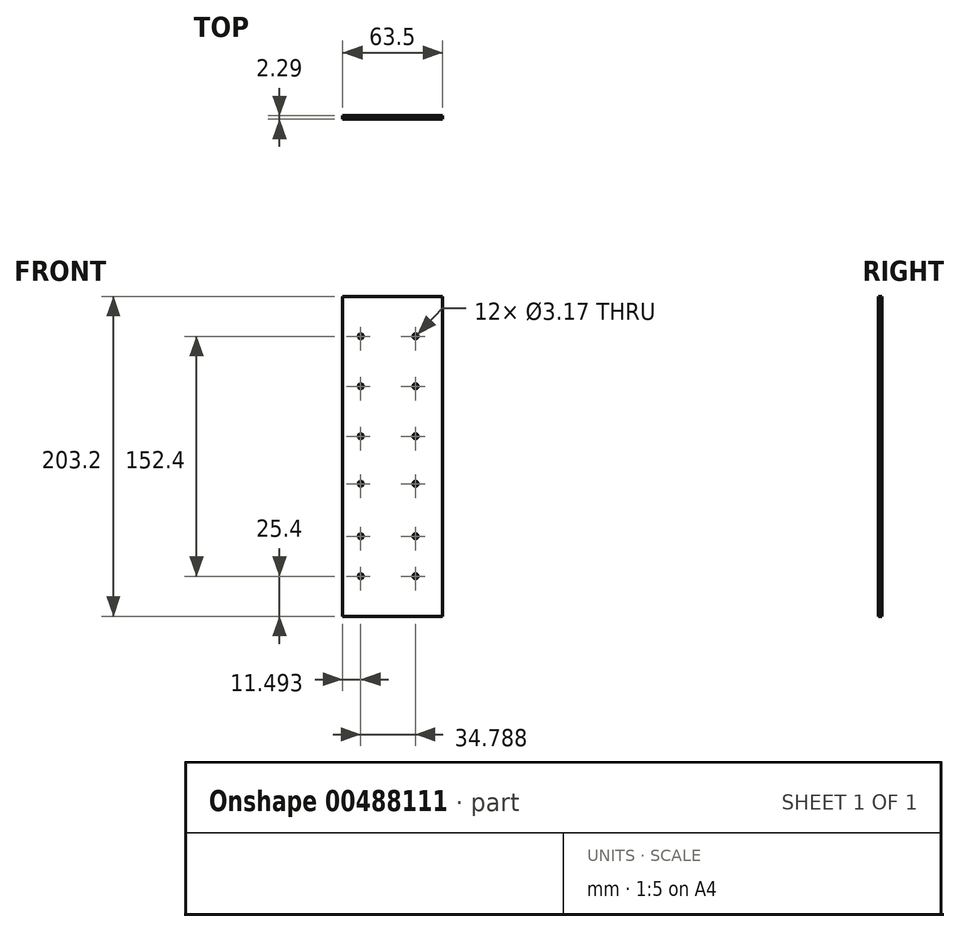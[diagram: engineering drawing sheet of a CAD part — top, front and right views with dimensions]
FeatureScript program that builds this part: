
annotation { "Feature Type Name" : "Feature", "Feature Type Description" : "" }
export const myFeature = defineFeature(function(context is Context, id is Id, definition is map)
    precondition{}
    {
        {
            var Q0;
            Q0=qCreatedBy(makeId("Front.planeOp"),FACE);
            var sketch = newSketch(context, id + "F0", { "sketchPlane" : qUnion([Q0])});
            skLineSegment(sketch, "E0.bottom", {"start": v(31.75, 101.6) * mm, "end": v(-31.75, 101.6) * mm});
            skLineSegment(sketch, "E0.top", {"start": v(31.75, -101.6) * mm, "end": v(-31.75, -101.6) * mm});
            skLineSegment(sketch, "E0.left", {"start": v(31.75, 101.6) * mm, "end": v(31.75, -101.6) * mm});
            skLineSegment(sketch, "E0.right", {"start": v(-31.75, 101.6) * mm, "end": v(-31.75, -101.6) * mm});
            skPoint(sketch, "E0.middle", {"position": v(0, 0) * mm});
            skCircle(sketch, "E1", {"center": v(-20.26, 76.2) * mm, "radius": 1.59 * mm});
            skCircle(sketch, "E2", {"center": v(-20.26, 44.45) * mm, "radius": 1.59 * mm});
            skCircle(sketch, "E3", {"center": v(-20.26, 12.7) * mm, "radius": 1.59 * mm});
            skCircle(sketch, "E4", {"center": v(-20.26, -17.46) * mm, "radius": 1.59 * mm});
            skCircle(sketch, "E5", {"center": v(-20.26, -50.8) * mm, "radius": 1.59 * mm});
            skCircle(sketch, "E6", {"center": v(-20.26, -76.2) * mm, "radius": 1.59 * mm});
            skCircle(sketch, "E7", {"center": v(14.53, 76.2) * mm, "radius": 1.59 * mm});
            skCircle(sketch, "E8", {"center": v(14.53, 44.45) * mm, "radius": 1.59 * mm});
            skCircle(sketch, "E9", {"center": v(14.53, 12.7) * mm, "radius": 1.59 * mm});
            skCircle(sketch, "E10", {"center": v(14.53, -17.46) * mm, "radius": 1.59 * mm});
            skCircle(sketch, "E11", {"center": v(14.53, -50.8) * mm, "radius": 1.59 * mm});
            skCircle(sketch, "E12", {"center": v(14.53, -76.2) * mm, "radius": 1.59 * mm});
            skSolve(sketch);
        }
        {
            var Q0;
            Q0=makeQuery(id+"F0.imprint","IMPRINT",FACE,{"disambiguationData":[TD([[makeQuery(id+"F0.imprint","IMPRINT",EDGE,{"derivedFrom":sQuery(id+"F0.wireOp",EDGE,"E0.bottom")}),1.0]])]});
            extrude(context, id + "F1", {"entities" : qUnion([Q0]), "depth" : 2.3 * mm});
        }
    });
